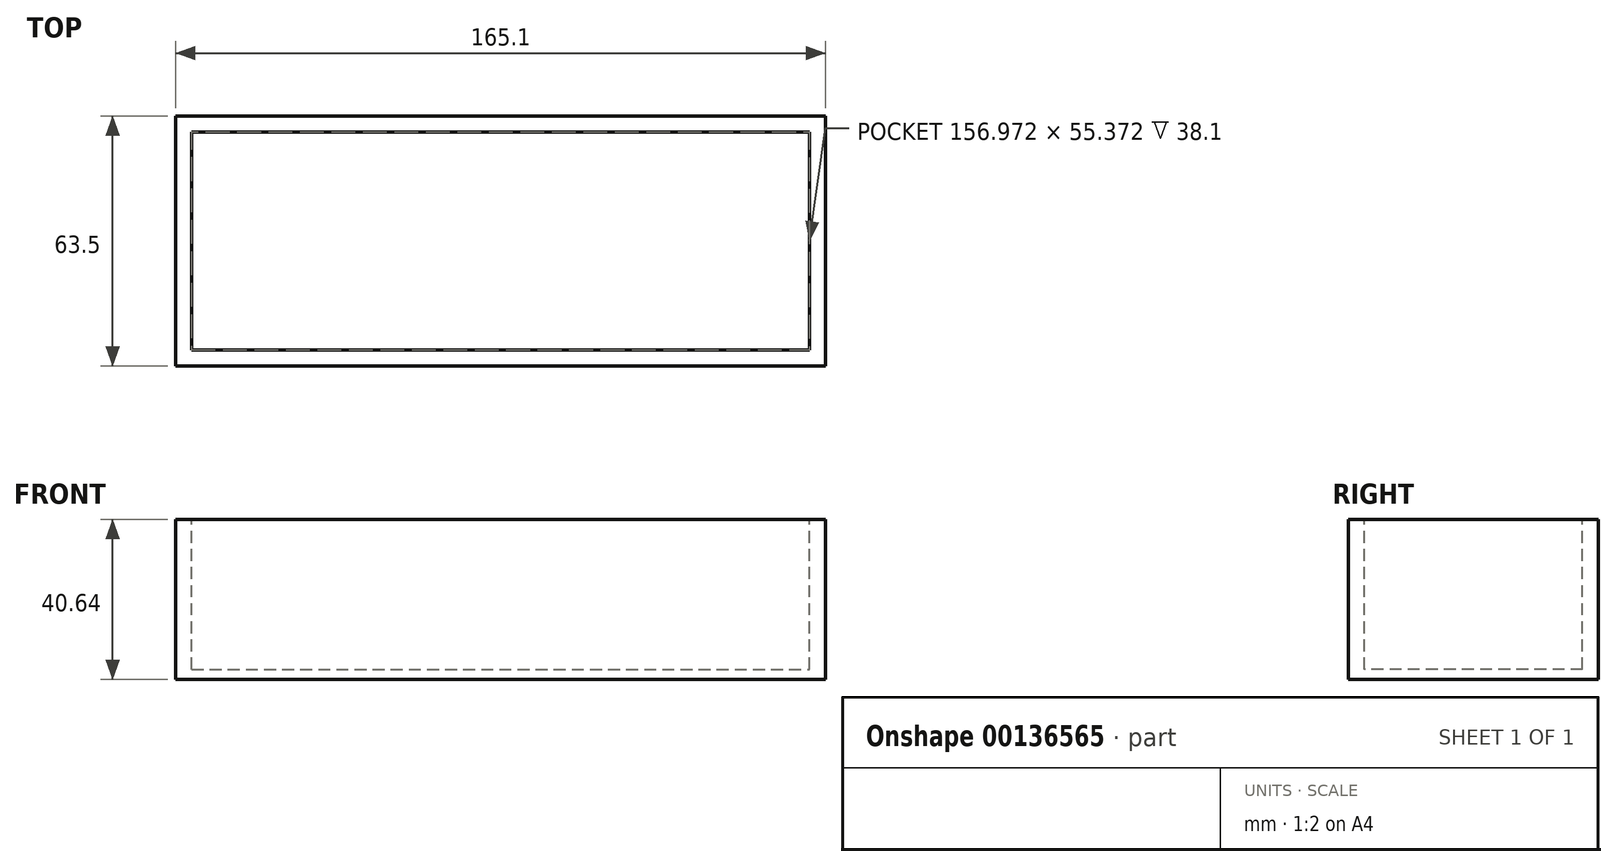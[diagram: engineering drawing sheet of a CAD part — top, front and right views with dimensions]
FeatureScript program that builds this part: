
annotation { "Feature Type Name" : "Feature", "Feature Type Description" : "" }
export const myFeature = defineFeature(function(context is Context, id is Id, definition is map)
    precondition{}
    {
        {
            var Q0;
            Q0=qCreatedBy(makeId("Front.planeOp"),FACE);
            var sketch = newSketch(context, id + "F0", { "sketchPlane" : qUnion([Q0])});
            skLineSegment(sketch, "E0.bottom", {"start": v(-82.55, 19.05) * mm, "end": v(82.55, 19.05) * mm});
            skLineSegment(sketch, "E0.top", {"start": v(-82.55, -19.05) * mm, "end": v(82.55, -19.05) * mm});
            skLineSegment(sketch, "E0.left", {"start": v(-82.55, 19.05) * mm, "end": v(-82.55, -19.05) * mm});
            skLineSegment(sketch, "E0.right", {"start": v(82.55, 19.05) * mm, "end": v(82.55, -19.05) * mm});
            skPoint(sketch, "E0.middle", {"position": v(0, 0) * mm});
            skSolve(sketch);
        }
        {
            var Q0;
            Q0=makeQuery(id+"F0.imprint","IMPRINT",FACE,{"disambiguationData":[TD([[makeQuery(id+"F0.imprint","IMPRINT",EDGE,{"derivedFrom":sQuery(id+"F0.wireOp",EDGE,"E0.bottom")}),-1.0]])]});
            extrude(context, id + "F1", {"entities" : qUnion([Q0]), "depth" : 63.5 * mm});
        }
        {
            var Q0;
            Q0=makeQuery(id+"F1.opExtrude","SWEPT_FACE",FACE,{"disambiguationData":[OSD([sQuery(id+"F0.wireOp",EDGE,"E0.bottom")])]});
            var sketch = newSketch(context, id + "F2", { "sketchPlane" : qUnion([Q0])});
            skLineSegment(sketch, "E1.bottom", {"start": v(-78.49, -4.06) * mm, "end": v(78.49, -4.06) * mm});
            skLineSegment(sketch, "E1.top", {"start": v(-78.49, -59.44) * mm, "end": v(78.49, -59.44) * mm});
            skLineSegment(sketch, "E1.left", {"start": v(-78.49, -4.06) * mm, "end": v(-78.49, -59.44) * mm});
            skLineSegment(sketch, "E1.right", {"start": v(78.49, -4.06) * mm, "end": v(78.49, -59.44) * mm});
            skSolve(sketch);
        }
        {
            var Q0;
            Q0=makeQuery(id+"F2.imprint","IMPRINT",FACE,{"disambiguationData":[TD([[makeQuery(id+"F2.imprint","IMPRINT",EDGE,{"derivedFrom":sQuery(id+"F2.wireOp",EDGE,"E1.bottom")}),-1.0]])]});
            extrude(context, id + "F3", {"entities" : qUnion([Q0]), "operationType" : NewBodyOperationType.REMOVE, "oppositeDirection" : true, "depth" : 46.74 * mm});
        }
        {
            var Q0;
            Q0=makeQuery(id+"F1.opExtrude","SWEPT_FACE",FACE,{"disambiguationData":[OSD([sQuery(id+"F0.wireOp",EDGE,"E0.top")])]});
            var sketch = newSketch(context, id + "F4", { "sketchPlane" : qUnion([Q0])});
            skLineSegment(sketch, "E2.bottom", {"start": v(-82.55, 0) * mm, "end": v(82.55, 0) * mm});
            skLineSegment(sketch, "E2.top", {"start": v(-82.55, 63.5) * mm, "end": v(82.55, 63.5) * mm});
            skLineSegment(sketch, "E2.left", {"start": v(-82.55, 0) * mm, "end": v(-82.55, 63.5) * mm});
            skLineSegment(sketch, "E2.right", {"start": v(82.55, 0) * mm, "end": v(82.55, 63.5) * mm});
            skSolve(sketch);
        }
        {
            var Q0;
            {var subQ0=makeQuery(id+"F1.opExtrude","SWEPT_FACE",FACE,{"disambiguationData":[OSD([sQuery(id+"F0.wireOp",EDGE,"E0.top")])]});Q0=makeQuery(id+"F4.imprint","IMPRINT",FACE,{"disambiguationData":[TD([[makeQuery(id+"F4.imprint","IMPRINT",EDGE,{"derivedFrom":makeQuery(id+"F3.boolean.opBoolean","INTERSECT",EDGE,{"derivedFrom":[subQ0,makeQuery(id+"F3.opExtrude","SWEPT_FACE",FACE,{"disambiguationData":[OSD([sQuery(id+"F2.wireOp",EDGE,"E1.bottom")])]})]})}),1.0]])]});}
            var Q1;
            Q1=makeQuery(id+"F4.imprint","IMPRINT",FACE,{"disambiguationData":[TD([[makeQuery(id+"F4.imprint","IMPRINT",EDGE,{"derivedFrom":sQuery(id+"F4.wireOp",EDGE,"E2.bottom")}),1.0]])]});
            extrude(context, id + "F5", {"entities" : qUnion([Q0, Q1]), "operationType" : NewBodyOperationType.ADD, "depth" : 2.54 * mm});
        }
    });
